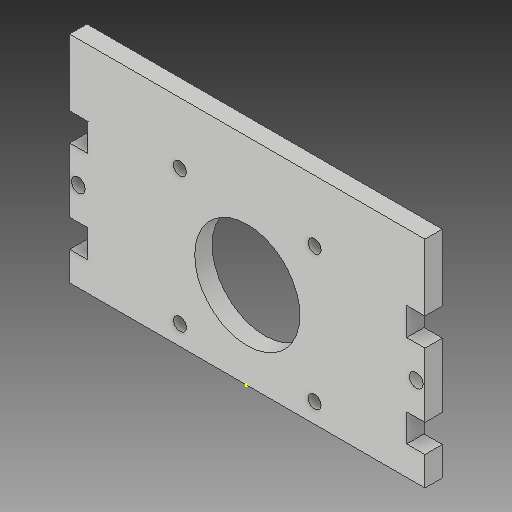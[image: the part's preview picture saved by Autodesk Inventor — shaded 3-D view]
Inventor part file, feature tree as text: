
AUTODESK INVENTOR PART (.ipt)
format: ipt  version: 2019 (Build 230136000, 136)  size: 174,080 bytes
history: native  units: in
note: dims shown in document units (in); Inventor stores cm internally (conversion verified against a paired STEP export)
features: reference x12, other x5, sketch x3, extrude x2, helix x1
ambient origin geometry x8: Origin, YZ Plane, XZ Plane, XY Plane, X Axis, Y Axis, Z Axis, Center Point
bodies: Solid1 (feature_tree)
feature tree (23):
  extrude  "Extrusion1"  Depth=0.1575in
  extrude  "Extrusion2"  Depth=0.0079in
  sketch  "Sketch3"  dims[d6=0.0079in d7=0.0079in d8=0.1575in d9=0.0in]
  sketch  "Sketch1"  dims[d0=0.1575in d1=0.0in d2=0.126in]
  reference  "Reference1"
  reference  "Reference2"
  reference  "Reference3"
  reference  "Reference4"
  reference  "Reference5"
  reference  "Reference6"
  sketch  "Sketch2"  dims[d3=0.126in d4=0.0079in d5=0.0079in]
  reference  "Reference7"
  reference  "Reference8"
  reference  "Reference9"
  reference  "Reference10"
  reference  "Reference11"
  reference  "Reference12"
  other  "<userpath>\Documents\CAD Files\Helix DLP\Helix DLP.iam"
  helix  "Helix DLP.iam"  [1 undecoded]
  other  "M1173041- NEMA 17 Screw rod:1"
  other  "Motor Brace_1:1"
  other  "motor_brace_3:2"
  other  "motor_brace_3:1"
note: 1 required parameter value undecoded (feature->parameter linkage not recoverable at this tier; creation-order binding heuristic only, values carry confidence <= 0.55)
